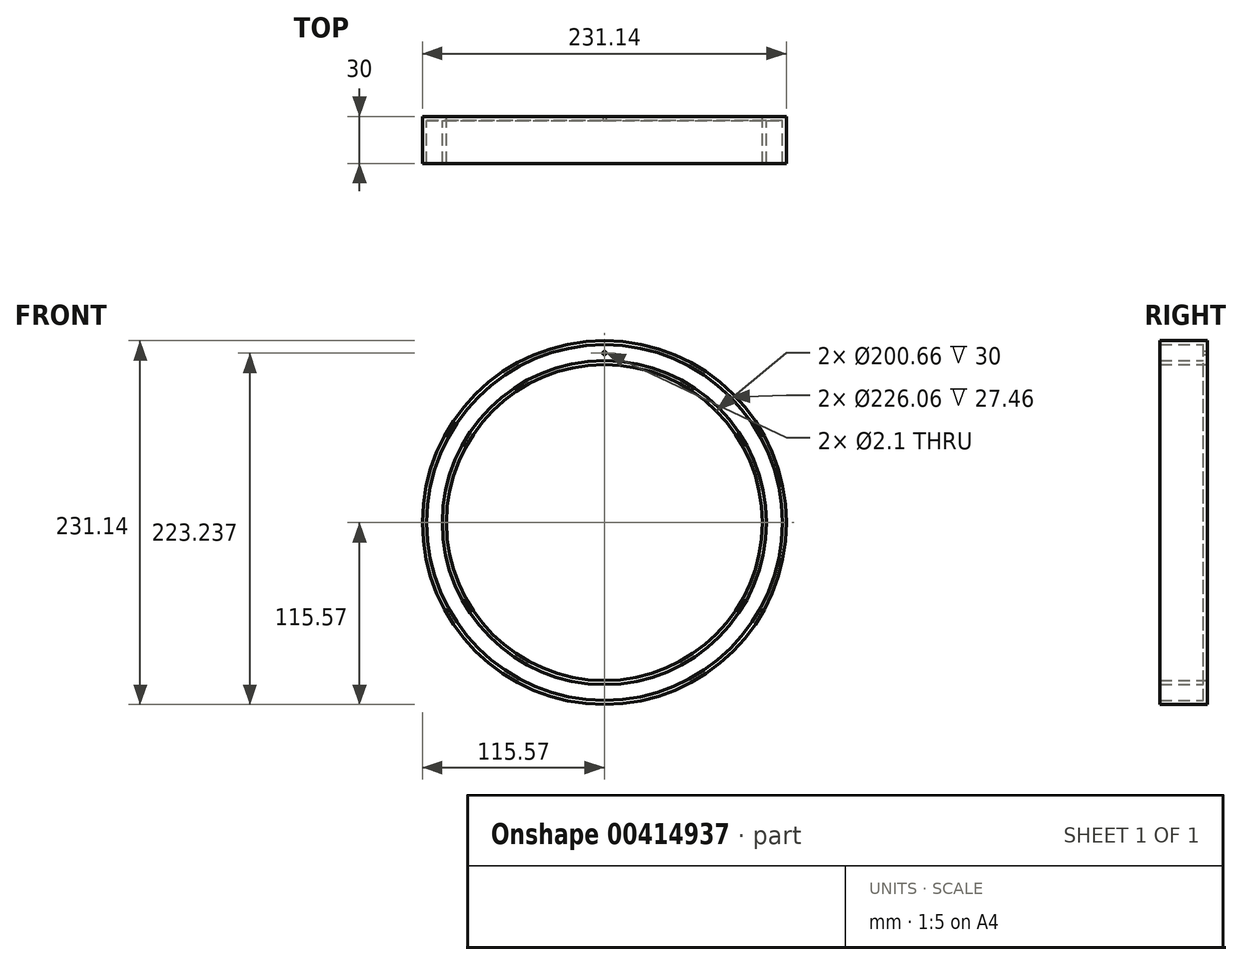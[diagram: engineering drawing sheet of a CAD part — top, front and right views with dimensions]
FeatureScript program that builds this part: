
annotation { "Feature Type Name" : "Feature", "Feature Type Description" : "" }
export const myFeature = defineFeature(function(context is Context, id is Id, definition is map)
    precondition{}
    {
        {
            var Q0;
            Q0=qCreatedBy(makeId("Front.planeOp"),FACE);
            var sketch = newSketch(context, id + "F0", { "sketchPlane" : qUnion([Q0])});
            skCircle(sketch, "E0", {"center": v(0, 0) * mm, "radius": 100.33 * mm});
            skCircle(sketch, "E1", {"center": v(0, 0) * mm, "radius": 115.57 * mm});
            skSolve(sketch);
        }
        {
            var Q0;
            Q0=makeQuery(id+"F0.imprint","IMPRINT",FACE,{"disambiguationData":[TD([[makeQuery(id+"F0.imprint","IMPRINT",EDGE,{"derivedFrom":sQuery(id+"F0.wireOp",EDGE,"E0")}),-1.0]])]});
            extrude(context, id + "F1", {"entities" : qUnion([Q0]), "depth" : 30 * mm});
        }
        {
            var Q0;
            Q0=makeQuery(id+"F1.opExtrude","CAP_FACE",FACE,{"disambiguationData":[OSD([sQuery(id+"F0.wireOp",EDGE,"E0"),sQuery(id+"F0.wireOp",EDGE,"E1")])],"isStart":false});
            var Q1;
            Q1=makeQuery(id+"F1.opExtrude","SWEPT_BODY",BODY,{"disambiguationData":[OSD([sQuery(id+"F0.wireOp",EDGE,"E0"),sQuery(id+"F0.wireOp",EDGE,"E1")])]});
            shell(context, id + "F2", {"entities" : qUnion([Q0]), "parts" : qUnion([Q1]), "thickness" : 2.54 * mm});
        }
        {
            var Q0;
            {var subQ0=sQuery(id+"F0.wireOp",EDGE,"E1");var subQ1=sQuery(id+"F0.wireOp",EDGE,"E0");Q0=makeQuery(id+"F2.opShell","OFFSET_FACE",FACE,{"disambiguationData":[OSD([subQ1,subQ0]),TDD([makeQuery(id+"F1.opExtrude","CAP_FACE",FACE,{"disambiguationData":[OSD([subQ1,subQ0])],"isStart":true})])]});}
            var sketch = newSketch(context, id + "F3", { "sketchPlane" : qUnion([Q0])});
            skPoint(sketch, "E2", {"position": v(0, 107.67) * mm});
            skSolve(sketch);
        }
        {
            var Q0;
            Q0=sQuery(id+"F3.wireOp",VERTEX,"E2");
            var Q1;
            Q1=makeQuery(id+"F1.opExtrude","SWEPT_BODY",BODY,{"disambiguationData":[OSD([sQuery(id+"F0.wireOp",EDGE,"E0"),sQuery(id+"F0.wireOp",EDGE,"E1")])]});
            hole(context, id + "F4", {"style" : HoleStyle.SIMPLE, "endStyle" : HoleEndStyle.THROUGH, "holeDiameter" : 2.1 * mm, "isTappedThrough" : true, "tappedDepth" : 12.7 * mm, "tapClearance" : 3, "locations" : qUnion([Q0]), "scope" : qUnion([Q1])});
        }
    });
